# Revit family: P500333-009
name_source: partatom
category: Lighting Fixtures
units: mm (PartAtom-declared; Revit-internal decimal feet)

## family parameters
Cut with Voids When Loaded = No
Host = Face
Light Source = Yes
OmniClass Number = 23.80.70.11.14.17
OmniClass Title = Direct/Indirect
Part Type = Normal
Room Calculation Point = No
Round Connector Dimension = Use Diameter
Shared = Yes

## types (1)
- P500333-009
    Apparent Load = 100 VA
    Assembly Code = D5020200
    Color Filter = 16777215
    Connector Description = Lighting Connector
    Default Elevation = 48 "
    Description = Merry Collection One-Light Brushed Nickel and Etched Glass Transitional Style Foyer Pendant Light
    Dimming Lamp Color Temperature Shift = <None>
    Features = Bring a modern vibe to any room with the Merry Collection 1-Light Brushed Nickel Etched Glass Transitional Foyer Pendant Light. The clean-lined frame, tubular arm, and round light base are coated in a silver brushed nickel finish. A light source glows from inside a crisp etched glass shade.
Application: Bring a modern vibe to any room with the Merry Collection 1-Light Brushed Nickel Etched Glass Transitional Foyer Pendant Light ideal for any foyer, dining room, stairway, or entryway.
Styles: Perfect for transitional and contemporary style settings.
Finish: The clean-lined frame, tubular arm, and round light base are coated in silver brushed nickel finish.
Materials: Constructed from steel to ensure a long product lifespan.
Glass/Shades: A light source glows from inside a crisp etched glass shade.
Bulbs: For ideal illumination, use 1 medium base bulb that is sold separately (100w max - LED/CFL/incandescent). Compatible with dimmable bulbs.
Dimensions: Measures 15-inch diameter by 23-inch height.
Certifications: cULus dry location listed.
Pairs With: Pairs with the Tobin, Etched Glass, and Dome Glass collections.
Warranty: Our 1-Year Limited Warranty guarantees your complete satisfaction with your purchase and includes professional after-sales customer service support.
    Fixture distribution = Direct
    Glass = Paint - Hubbell - White Texture
    Gold = Hubbell - Gold
    Housing Material = Paint - Hubbell - Nickel
    Lamp = LED/CFL/incandescent
    Load Classification = Lighting
    Manufacturer = Progress Lighting
    Model = P500333-009
    Photometric Web File = generic
    Power Factor = 1
    Product Documentation Link = https://hubbellcdn.com
    Product Link = https://www.hubbell.com
    Tilt Angle = 60.00°
    URL = https://www.hubbell.com
    Voltage = 120 V
    Warranty = 1 year Warranty
    Wattage Comments = 100W
    Watts = 100 W

## geometry (parser evidence)
native form markers: Sweep x2
no freeform markers — native parametric forms only
